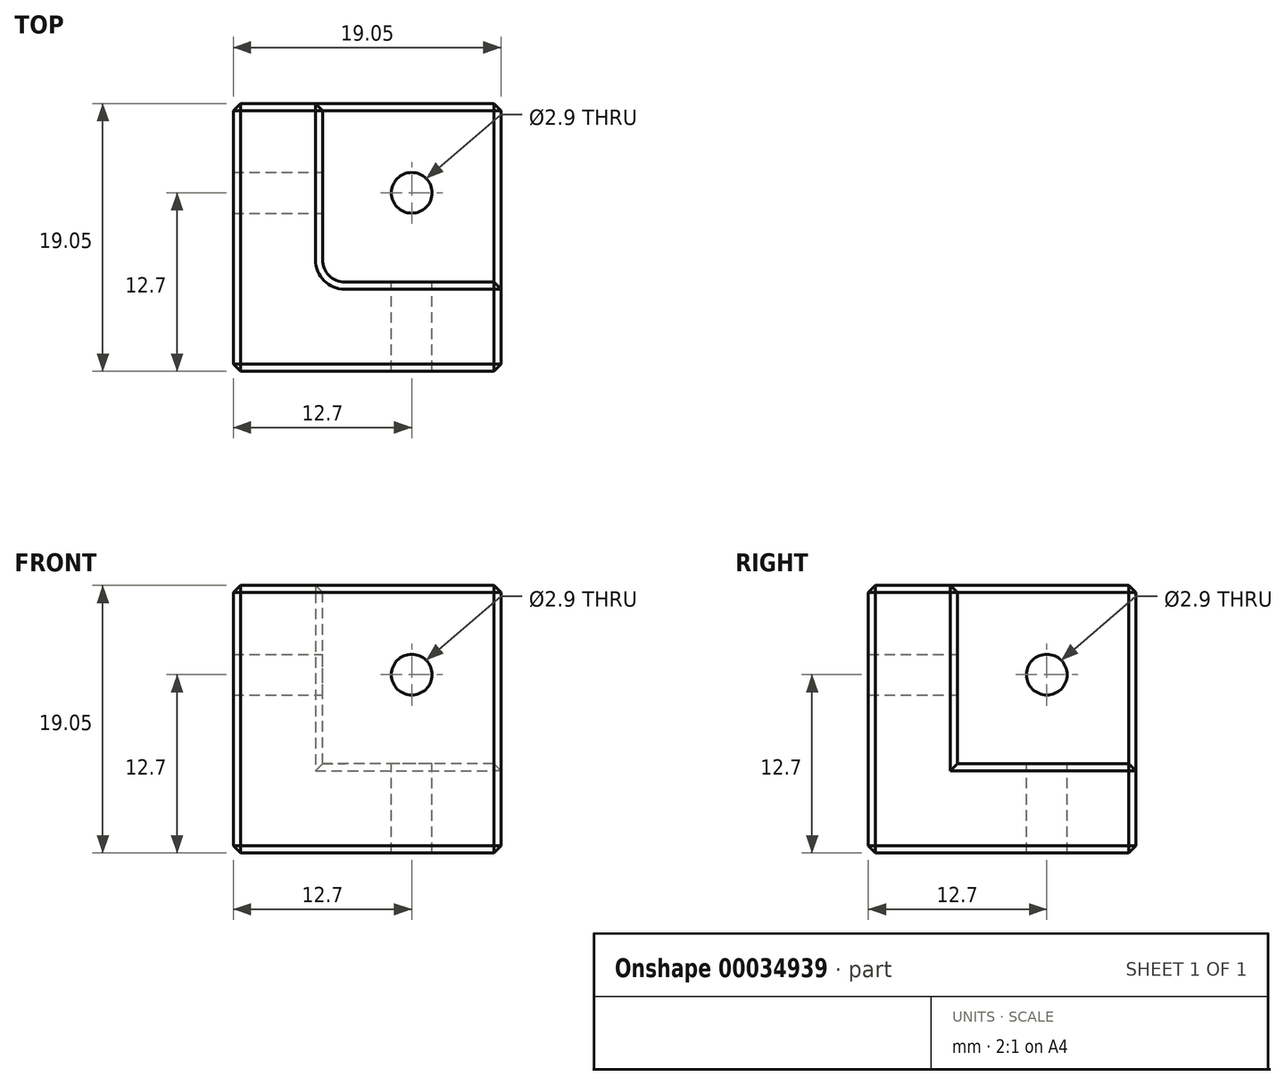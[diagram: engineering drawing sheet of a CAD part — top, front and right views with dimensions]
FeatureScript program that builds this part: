
annotation { "Feature Type Name" : "Feature", "Feature Type Description" : "" }
export const myFeature = defineFeature(function(context is Context, id is Id, definition is map)
    precondition{}
    {
        {
            var Q0;
            Q0=qCreatedBy(makeId("Top.planeOp"),FACE);
            var sketch = newSketch(context, id + "F0", { "sketchPlane" : qUnion([Q0])});
            skLineSegment(sketch, "E0.bottom", {"start": v(0, 0) * mm, "end": v(19.05, 0) * mm});
            skLineSegment(sketch, "E0.top", {"start": v(0, 19.05) * mm, "end": v(19.05, 19.05) * mm});
            skLineSegment(sketch, "E0.left", {"start": v(0, 0) * mm, "end": v(0, 19.05) * mm});
            skLineSegment(sketch, "E0.right", {"start": v(19.05, 0) * mm, "end": v(19.05, 19.05) * mm});
            skSolve(sketch);
        }
        {
            var Q0;
            Q0=makeQuery(id+"F0.imprint","IMPRINT",FACE,{"disambiguationData":[TD([[makeQuery(id+"F0.imprint","IMPRINT",EDGE,{"derivedFrom":sQuery(id+"F0.wireOp",EDGE,"E0.bottom")}),1.0]])]});
            extrude(context, id + "F1", {"entities" : qUnion([Q0]), "depth" : 6.35 * mm});
        }
        {
            var Q0;
            Q0=makeQuery(id+"F1.opExtrude","CAP_FACE",FACE,{"disambiguationData":[OSD([sQuery(id+"F0.wireOp",EDGE,"E0.bottom"),sQuery(id+"F0.wireOp",EDGE,"E0.top"),sQuery(id+"F0.wireOp",EDGE,"E0.left"),sQuery(id+"F0.wireOp",EDGE,"E0.right")])],"isStart":false});
            var sketch = newSketch(context, id + "F2", { "sketchPlane" : qUnion([Q0])});
            skLineSegment(sketch, "E1", {"start": v(0, 19.05) * mm, "end": v(0, 0) * mm});
            skLineSegment(sketch, "E2", {"start": v(0, 0) * mm, "end": v(19.05, 0) * mm});
            skLineSegment(sketch, "E3", {"start": v(19.05, 0) * mm, "end": v(19.05, 6.35) * mm});
            skLineSegment(sketch, "E4", {"start": v(19.05, 6.35) * mm, "end": v(6.35, 6.35) * mm});
            skLineSegment(sketch, "E5", {"start": v(6.35, 6.35) * mm, "end": v(6.35, 19.05) * mm});
            skLineSegment(sketch, "E6", {"start": v(6.35, 19.05) * mm, "end": v(0, 19.05) * mm});
            skSolve(sketch);
        }
        {
            var Q0;
            Q0 = qSketchRegion(id + "F2", true);
            extrude(context, id + "F3", {"entities" : qUnion([Q0]), "operationType" : NewBodyOperationType.ADD, "depth" : 12.7 * mm});
        }
        {
            var Q0;
            Q0=makeQuery(id+"F3.opExtrude","SWEPT_FACE",FACE,{"disambiguationData":[OSD([sQuery(id+"F2.wireOp",EDGE,"E5")])]});
            var sketch = newSketch(context, id + "F4", { "sketchPlane" : qUnion([Q0])});
            skPoint(sketch, "E7", {"position": v(12.7, 12.7) * mm});
            skPoint(sketch, "E7.positionSnap0", {"position": v(6.35, 12.7) * mm});
            skPoint(sketch, "E7.positionSnap1", {"position": v(12.7, 19.05) * mm});
            skSolve(sketch);
        }
        {
            var Q0;
            Q0=makeQuery(id+"F1.opExtrude","CAP_FACE",FACE,{"disambiguationData":[OSD([sQuery(id+"F0.wireOp",EDGE,"E0.bottom"),sQuery(id+"F0.wireOp",EDGE,"E0.top"),sQuery(id+"F0.wireOp",EDGE,"E0.left"),sQuery(id+"F0.wireOp",EDGE,"E0.right")])],"isStart":false});
            var sketch = newSketch(context, id + "F5", { "sketchPlane" : qUnion([Q0])});
            skPoint(sketch, "E8", {"position": v(12.7, 12.7) * mm});
            skPoint(sketch, "E8.positionSnap0", {"position": v(19.05, 12.7) * mm});
            skPoint(sketch, "E8.positionSnap1", {"position": v(12.7, 19.05) * mm});
            skSolve(sketch);
        }
        {
            var Q0;
            Q0=makeQuery(id+"F3.opExtrude","SWEPT_FACE",FACE,{"disambiguationData":[OSD([sQuery(id+"F2.wireOp",EDGE,"E4")])]});
            var sketch = newSketch(context, id + "F6", { "sketchPlane" : qUnion([Q0])});
            skPoint(sketch, "E9", {"position": v(-12.7, 12.7) * mm});
            skPoint(sketch, "E9.positionSnap0", {"position": v(-19.05, 12.7) * mm});
            skPoint(sketch, "E9.positionSnap1", {"position": v(-12.7, 19.05) * mm});
            skSolve(sketch);
        }
        {
            var Q0;
            Q0=sQuery(id+"F4.wireOp",VERTEX,"E7");
            var Q1;
            Q1=sQuery(id+"F6.wireOp",VERTEX,"E9");
            var Q2;
            Q2=sQuery(id+"F5.wireOp",VERTEX,"E8");
            var Q3;
            Q3=makeQuery(id+"F1.opExtrude","SWEPT_BODY",BODY,{"disambiguationData":[OSD([sQuery(id+"F0.wireOp",EDGE,"E0.bottom"),sQuery(id+"F0.wireOp",EDGE,"E0.top"),sQuery(id+"F0.wireOp",EDGE,"E0.left"),sQuery(id+"F0.wireOp",EDGE,"E0.right")])]});
            hole(context, id + "F7", {"style" : HoleStyle.SIMPLE, "holeDiameter" : 2.9 * mm, "endStyle" : HoleEndStyle.THROUGH, "locations" : qUnion([Q0, Q1, Q2]), "scope" : qUnion([Q3])});
        }
        {
            var Q0;
            Q0=makeQuery(id+"F3.opExtrude","SWEPT_EDGE",EDGE,{"disambiguationData":[OSD([sQuery(id+"F2.wireOp",EDGE,"E4"),sQuery(id+"F2.wireOp",EDGE,"E5")])]});
            fillet(context, id + "F8", {"entities" : qUnion([Q0]), "radius" : 1.59 * mm, "tangentPropagation" : true, "allowEdgeOverflow" : false});
        }
        {
            var Q0;
            Q0=makeQuery(id+"F1.opExtrude","SWEPT_EDGE",EDGE,{"disambiguationData":[OSD([sQuery(id+"F0.wireOp",EDGE,"E0.top"),sQuery(id+"F0.wireOp",EDGE,"E0.right")])]});
            var Q1;
            Q1=makeQuery(id+"F1.opExtrude","CAP_EDGE",EDGE,{"disambiguationData":[OSD([sQuery(id+"F0.wireOp",EDGE,"E0.top")])],"isStart":false});
            var Q2;
            Q2=makeQuery(id+"F3.opExtrude","SWEPT_EDGE",EDGE,{"disambiguationData":[OSD([sQuery(id+"F0.wireOp",EDGE,"E0.top"),sQuery(id+"F2.wireOp",EDGE,"E5"),sQuery(id+"F2.wireOp",EDGE,"E6")])]});
            var Q3;
            Q3=makeQuery(id+"F3.boolean.opBoolean","MERGE",EDGE,{"derivedFrom":[makeQuery(id+"F1.opExtrude","SWEPT_EDGE",EDGE,{"disambiguationData":[OSD([sQuery(id+"F0.wireOp",EDGE,"E0.top"),sQuery(id+"F0.wireOp",EDGE,"E0.left")])]}),makeQuery(id+"F3.opExtrude","SWEPT_EDGE",EDGE,{"disambiguationData":[OSD([sQuery(id+"F2.wireOp",EDGE,"E1"),sQuery(id+"F2.wireOp",EDGE,"E6")])]})]});
            var Q4;
            Q4=makeQuery(id+"F3.opExtrude","CAP_EDGE",EDGE,{"disambiguationData":[OSD([sQuery(id+"F2.wireOp",EDGE,"E6")])],"isStart":false});
            var Q5;
            Q5=makeQuery(id+"F3.opExtrude","CAP_EDGE",EDGE,{"disambiguationData":[OSD([sQuery(id+"F2.wireOp",EDGE,"E5")])],"isStart":false});
            var Q6;
            Q6=makeQuery(id+"F3.opExtrude","SWEPT_EDGE",EDGE,{"disambiguationData":[OSD([sQuery(id+"F0.wireOp",EDGE,"E0.right"),sQuery(id+"F2.wireOp",EDGE,"E3"),sQuery(id+"F2.wireOp",EDGE,"E4")])]});
            var Q7;
            Q7=makeQuery(id+"F1.opExtrude","CAP_EDGE",EDGE,{"disambiguationData":[OSD([sQuery(id+"F0.wireOp",EDGE,"E0.right")])],"isStart":false});
            var Q8;
            Q8=makeQuery(id+"F3.boolean.opBoolean","MERGE",EDGE,{"derivedFrom":[makeQuery(id+"F1.opExtrude","SWEPT_EDGE",EDGE,{"disambiguationData":[OSD([sQuery(id+"F0.wireOp",EDGE,"E0.bottom"),sQuery(id+"F0.wireOp",EDGE,"E0.right")])]}),makeQuery(id+"F3.opExtrude","SWEPT_EDGE",EDGE,{"disambiguationData":[OSD([sQuery(id+"F2.wireOp",EDGE,"E2"),sQuery(id+"F2.wireOp",EDGE,"E3")])]})]});
            var Q9;
            Q9=makeQuery(id+"F3.opExtrude","CAP_EDGE",EDGE,{"disambiguationData":[OSD([sQuery(id+"F2.wireOp",EDGE,"E3")])],"isStart":false});
            var Q10;
            Q10=makeQuery(id+"F3.opExtrude","CAP_EDGE",EDGE,{"disambiguationData":[OSD([sQuery(id+"F2.wireOp",EDGE,"E4")])],"isStart":false});
            var Q11;
            {var subQ0=sQuery(id+"F2.wireOp",EDGE,"E4");var subQ1=sQuery(id+"F2.wireOp",EDGE,"E5");Q11=makeQuery(id+"F8.opFillet","BLEND_EDGE",EDGE,{"blendedFrom":[makeQuery(id+"F3.opExtrude","SWEPT_EDGE",EDGE,{"disambiguationData":[OSD([subQ0,subQ1])]}),makeQuery(id+"F3.opExtrude","CAP_FACE",FACE,{"disambiguationData":[OSD([sQuery(id+"F2.wireOp",EDGE,"E1"),sQuery(id+"F2.wireOp",EDGE,"E2"),sQuery(id+"F2.wireOp",EDGE,"E3"),subQ0,subQ1,sQuery(id+"F2.wireOp",EDGE,"E6")])],"isStart":false})],"blendedInto":[makeQuery(id+"F3.opExtrude","CAP_FACE",FACE,{"disambiguationData":[OSD([sQuery(id+"F2.wireOp",EDGE,"E1"),sQuery(id+"F2.wireOp",EDGE,"E2"),sQuery(id+"F2.wireOp",EDGE,"E3"),subQ0,subQ1,sQuery(id+"F2.wireOp",EDGE,"E6")])],"isStart":false})]});}
            var Q12;
            Q12=makeQuery(id+"F3.opExtrude","CAP_EDGE",EDGE,{"disambiguationData":[OSD([sQuery(id+"F2.wireOp",EDGE,"E2")])],"isStart":false});
            var Q13;
            Q13=makeQuery(id+"F3.opExtrude","CAP_EDGE",EDGE,{"disambiguationData":[OSD([sQuery(id+"F2.wireOp",EDGE,"E1")])],"isStart":false});
            var Q14;
            Q14=makeQuery(id+"F3.boolean.opBoolean","MERGE",EDGE,{"derivedFrom":[makeQuery(id+"F1.opExtrude","SWEPT_EDGE",EDGE,{"disambiguationData":[OSD([sQuery(id+"F0.wireOp",EDGE,"E0.bottom"),sQuery(id+"F0.wireOp",EDGE,"E0.left")])]}),makeQuery(id+"F3.opExtrude","SWEPT_EDGE",EDGE,{"disambiguationData":[OSD([sQuery(id+"F2.wireOp",EDGE,"E1"),sQuery(id+"F2.wireOp",EDGE,"E2")])]})]});
            var Q15;
            Q15=makeQuery(id+"F1.opExtrude","CAP_EDGE",EDGE,{"disambiguationData":[OSD([sQuery(id+"F0.wireOp",EDGE,"E0.right")])],"isStart":true});
            var Q16;
            Q16=makeQuery(id+"F1.opExtrude","CAP_EDGE",EDGE,{"disambiguationData":[OSD([sQuery(id+"F0.wireOp",EDGE,"E0.top")])],"isStart":true});
            var Q17;
            Q17=makeQuery(id+"F1.opExtrude","CAP_EDGE",EDGE,{"disambiguationData":[OSD([sQuery(id+"F0.wireOp",EDGE,"E0.left")])],"isStart":true});
            var Q18;
            Q18=makeQuery(id+"F1.opExtrude","CAP_EDGE",EDGE,{"disambiguationData":[OSD([sQuery(id+"F0.wireOp",EDGE,"E0.bottom")])],"isStart":true});
            chamfer(context, id + "F9", {"entities" : qUnion([Q0, Q1, Q2, Q3, Q4, Q5, Q6, Q7, Q8, Q9, Q10, Q11, Q12, Q13, Q14, Q15, Q16, Q17, Q18]), "width" : 0.5 * mm, "tangentPropagation" : true});
        }
    });
